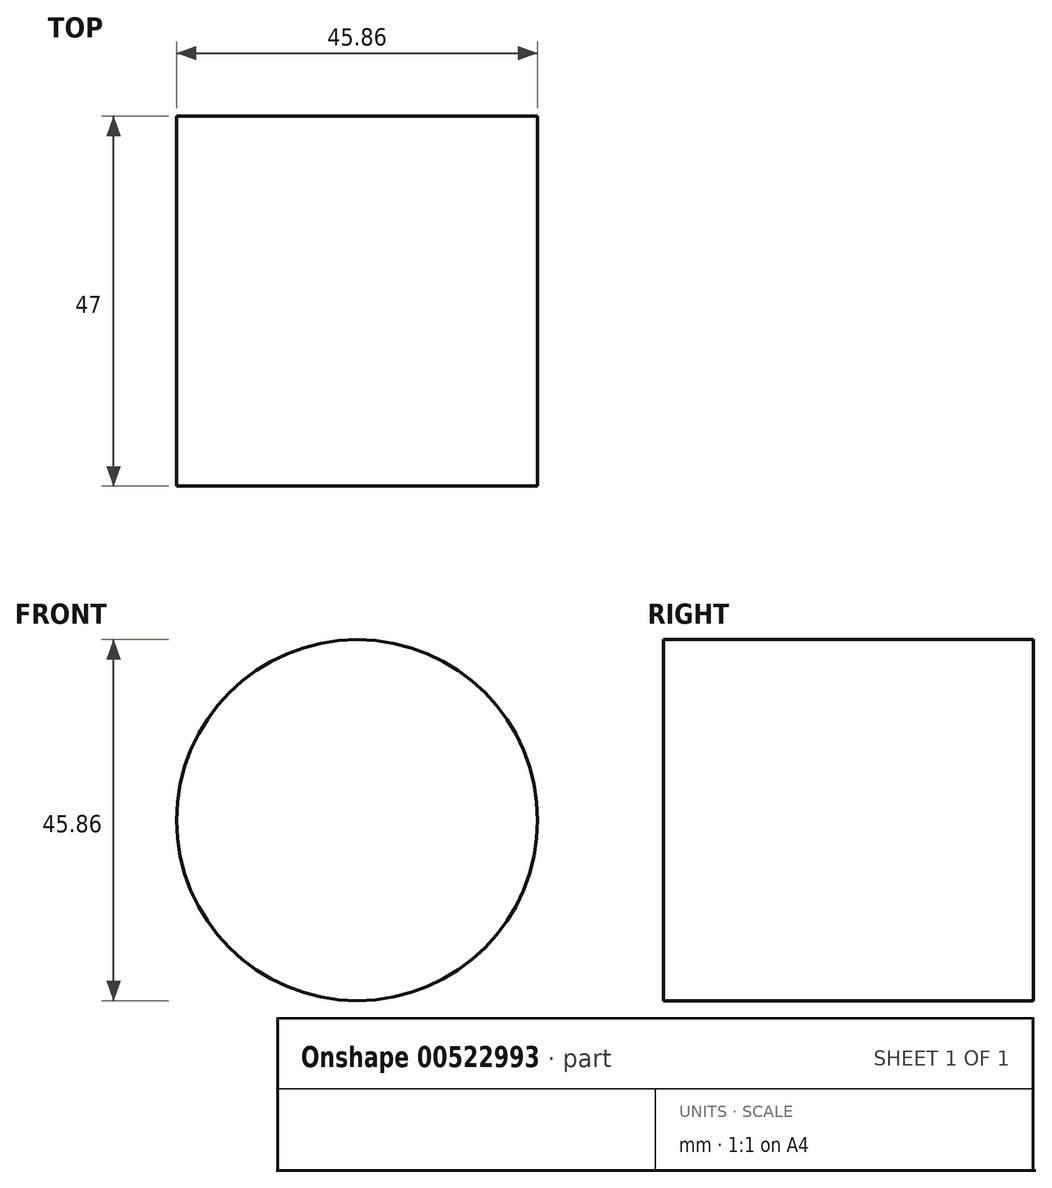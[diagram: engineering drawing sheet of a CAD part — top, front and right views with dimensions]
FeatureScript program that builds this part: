
annotation { "Feature Type Name" : "Feature", "Feature Type Description" : "" }
export const myFeature = defineFeature(function(context is Context, id is Id, definition is map)
    precondition{}
    {
        {
            var Q0;
            Q0=qCreatedBy(makeId("Front.planeOp"),FACE);
            var sketch = newSketch(context, id + "F0", { "sketchPlane" : qUnion([Q0])});
            skCircle(sketch, "E0", {"center": v(0, 0) * mm, "radius": 22.93 * mm});
            skSolve(sketch);
        }
        {
            var Q0;
            Q0 = qSketchRegion(id + "F0", true);
            extrude(context, id + "F1", {"entities" : qUnion([Q0]), "depth" : 47 * mm, "offsetDistance" : 25 * mm});
        }
    });
